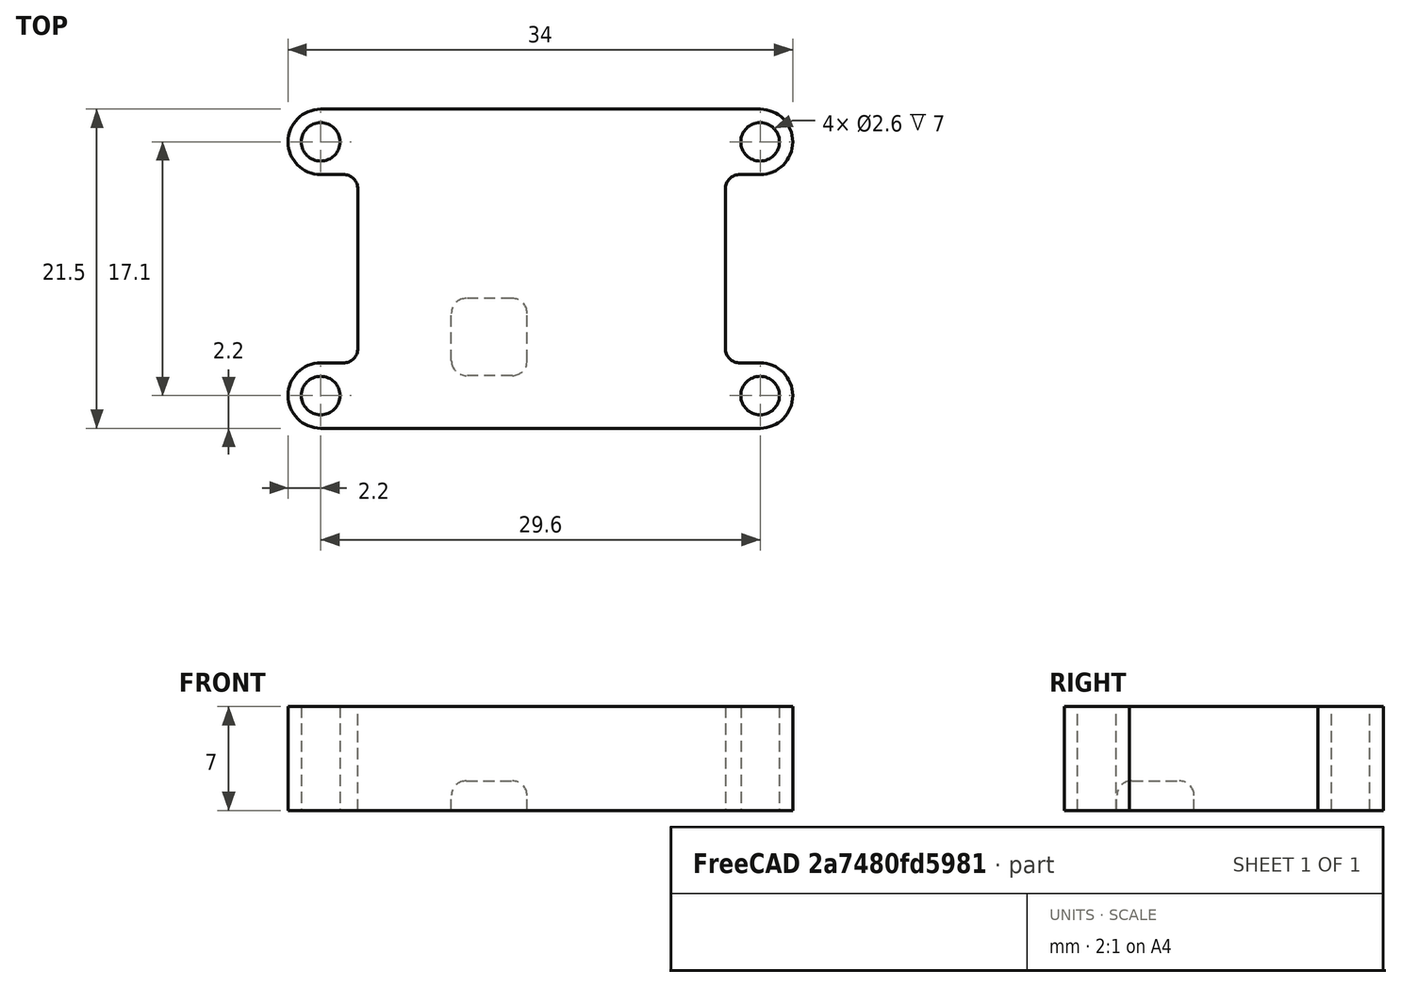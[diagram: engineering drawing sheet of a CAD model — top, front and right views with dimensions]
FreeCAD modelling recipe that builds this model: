
FCSTD DOCUMENT  (FreeCAD 0.21R33694 (Git))
Label: heatsink
License: All rights reserved
LicenseURL: http://en.wikipedia.org/wiki/All_rights_reserved
objects: Part::Cylinder×8, Part::Box×6, Part::Cut×5, Part::Fuse×4, Part::MultiFuse×1, Part::Fillet×1
note: 25 computed .brp shape members not serialized (recipe doc carries the construction recipe); baked Part::Feature solids carry a one-line shape summary decoded from their .brp

FEATURE [Part::Cylinder] cylinder
  Angle = 360
  AttacherType = Attacher::AttachEngine3D
  FirstAngle = 0
  Height = 7
  Radius = 2.2
  SecondAngle = 0
FEATURE [Part::Box] cube
  AttacherType = Attacher::AttachEngine3D
  Height = 7
  Length = 4.4
  Placement = pos=(-2.2,0,0) rot=(0,0,1;0rad)
  Width = 5
FEATURE [Part::Fuse] union
  Base = -> cylinder
  Tool = -> cube
FEATURE [Part::Cylinder] cylinder001
  Angle = 360
  AttacherType = Attacher::AttachEngine3D
  FirstAngle = 0
  Height = 7.1
  Placement = pos=(0,0,-0.01) rot=(0,0,1;0rad)
  Radius = 1.3
  SecondAngle = 0
FEATURE [Part::Cut] difference
  Base = -> union
  Placement = pos=(0,0,0) rot=(0,0,-1;1.5708rad)
  Tool = -> cylinder001
FEATURE [Part::Cylinder] cylinder002
  Angle = 360
  AttacherType = Attacher::AttachEngine3D
  FirstAngle = 0
  Height = 7
  Radius = 2.2
  SecondAngle = 0
FEATURE [Part::Box] cube001
  AttacherType = Attacher::AttachEngine3D
  Height = 7
  Length = 4.4
  Placement = pos=(-2.2,0,0) rot=(0,0,1;0rad)
  Width = 5
FEATURE [Part::Fuse] union001
  Base = -> cylinder002
  Tool = -> cube001
FEATURE [Part::Cylinder] cylinder003
  Angle = 360
  AttacherType = Attacher::AttachEngine3D
  FirstAngle = 0
  Height = 7.1
  Placement = pos=(0,0,-0.01) rot=(0,0,1;0rad)
  Radius = 1.3
  SecondAngle = 0
FEATURE [Part::Cut] difference001
  Base = -> union001
  Placement = pos=(29.6,0,0) rot=(0,0,1;1.5708rad)
  Tool = -> cylinder003
FEATURE [Part::Cylinder] cylinder004
  Angle = 360
  AttacherType = Attacher::AttachEngine3D
  FirstAngle = 0
  Height = 7
  Radius = 2.2
  SecondAngle = 0
FEATURE [Part::Box] cube002
  AttacherType = Attacher::AttachEngine3D
  Height = 7
  Length = 4.4
  Placement = pos=(-2.2,0,0) rot=(0,0,1;0rad)
  Width = 5
FEATURE [Part::Fuse] union002
  Base = -> cylinder004
  Tool = -> cube002
FEATURE [Part::Cylinder] cylinder005
  Angle = 360
  AttacherType = Attacher::AttachEngine3D
  FirstAngle = 0
  Height = 7.1
  Placement = pos=(0,0,-0.01) rot=(0,0,1;0rad)
  Radius = 1.3
  SecondAngle = 0
FEATURE [Part::Cut] difference002
  Base = -> union002
  Placement = pos=(29.6,17.1,0) rot=(0,0,1;1.5708rad)
  Tool = -> cylinder005
FEATURE [Part::Cylinder] cylinder006
  Angle = 360
  AttacherType = Attacher::AttachEngine3D
  FirstAngle = 0
  Height = 7
  Radius = 2.2
  SecondAngle = 0
FEATURE [Part::Box] cube003
  AttacherType = Attacher::AttachEngine3D
  Height = 7
  Length = 4.4
  Placement = pos=(-2.2,0,0) rot=(0,0,1;0rad)
  Width = 5
FEATURE [Part::Fuse] union003
  Base = -> cylinder006
  Tool = -> cube003
FEATURE [Part::Cylinder] cylinder007
  Angle = 360
  AttacherType = Attacher::AttachEngine3D
  FirstAngle = 0
  Height = 7.1
  Placement = pos=(0,0,-0.01) rot=(0,0,1;0rad)
  Radius = 1.3
  SecondAngle = 0
FEATURE [Part::Cut] difference003
  Base = -> union003
  Placement = pos=(0,17.1,0) rot=(0,0,-1;1.5708rad)
  Tool = -> cylinder007
FEATURE [Part::Box] cube004
  AttacherType = Attacher::AttachEngine3D
  Height = 7
  Length = 24.75
  Placement = pos=(2.5,-2.2,0) rot=(0,0,1;0rad)
  Width = 21.5
FEATURE [Part::MultiFuse] union004
  Shapes = -> [difference,difference001,difference002,difference003,cube004]
FEATURE [Part::Box] cube005
  AttacherType = Attacher::AttachEngine3D
  Height = 2
  Length = 5.1
  Placement = pos=(8.8,1.35,-0.01) rot=(0,0,1;0rad)
  Width = 5.2
FEATURE [Part::Cut] difference004
  Base = -> union004
  Tool = -> cube005
FEATURE [Part::Fillet] Fillet
  Base = -> difference004
  Edges = 12 edges r=1: [Edge36,Edge39,Edge50,Edge51,Edge52,Edge53,Edge54,Edge55,Edge56,Edge57,Edge58,Edge59]
